# Revit family: 26753
name_source: partatom
category: Aparatos sanitarios
revit_build: Autodesk Revit 2017 (Build: 20160225_1515(x64)
units: mm (PartAtom-declared; Revit-internal decimal feet)

## family parameters
Anfitrión = Cara
Compartido = No
Corte con vacíos al cargar = No
Cota de conector redondo = Diámetro de uso
Número OmniClass = 23.45.55.14
Punto de cálculo de habitación = No
Tipo de pieza = Normal
Título OmniClass = Single Faucets

## types (1)
- 26753
    Accionamiento = Mediante pulsador
    CAUDAL = 15 l/min
    CIERRE = Automático en 6 seg.
    Comentarios de tipo = Cuerpo y pulsador en latón. Piezas inferiores en matieriales resistentes a la corrosión e incrustaciones calcáreas. Cabeza intercambiable.Suministrado con llave de paso y caja para empotrar, latiguillos flexibles en acero inoxidable de  1/2". Caudal regulabre en función de la presión.
    Conexión AC = No
    Conexión AF = Sí
    Código de montaje = C1030220
    Descripción = Grifo temporalizado de un agua para instalación mural y apertura por pulsador.
    ENTRADA = Con latiguillos flexibles de 1/2"
    Elevación por defecto = 1219 mm
    Fabricante = PRESTO IBÉRICA
    Imagen de tipo = <Ninguno>
    Material = <Por categoría>
    Modelo = PRESTO XT 2000 - UE Inox
    PESO BRUTO = 1,100 Kg
    Presión Máxima = 8 bar.
    REFERENCIA = 26753
    TIPO DE AGUA = Fria
    Teléfono = (+34) 915 782 575
    URL = http://www.griferiasgalindo.com
